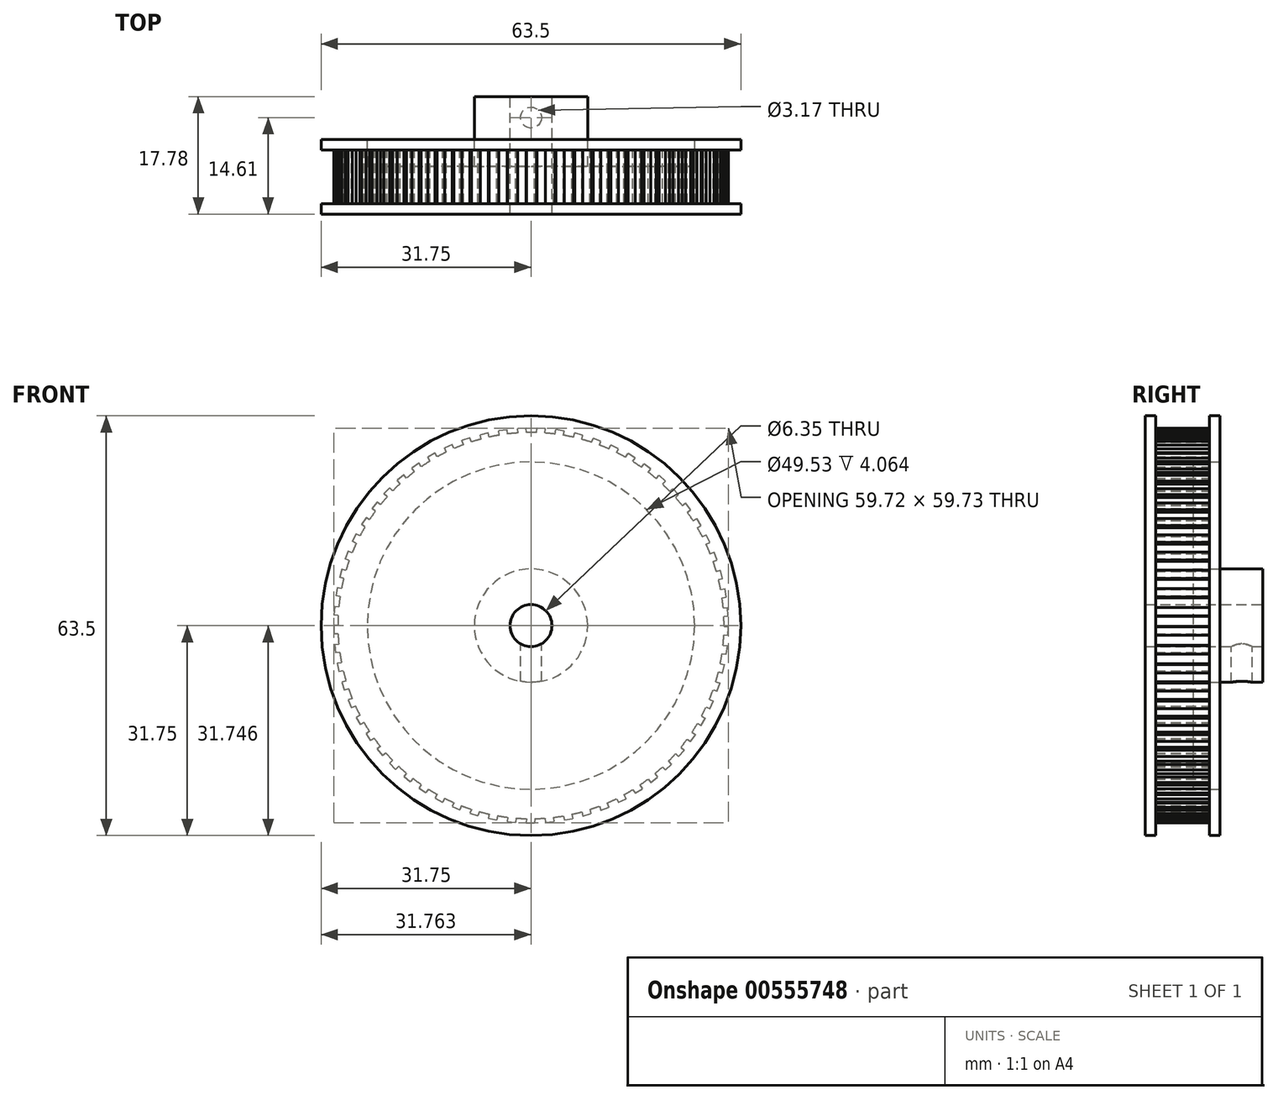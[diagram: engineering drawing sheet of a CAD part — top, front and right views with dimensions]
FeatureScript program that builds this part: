
annotation { "Feature Type Name" : "Feature", "Feature Type Description" : "" }
export const myFeature = defineFeature(function(context is Context, id is Id, definition is map)
    precondition{}
    {
        {
            var Q0;
            Q0=qCreatedBy(makeId("Front.planeOp"),FACE);
            var sketch = newSketch(context, id + "F0", { "sketchPlane" : qUnion([Q0])});
            skCircle(sketch, "E0", {"center": v(0, 0) * mm, "radius": 29.21 * mm});
            skSolve(sketch);
        }
        {
            var Q0;
            Q0=makeQuery(id+"F0.imprint","IMPRINT",FACE,{"disambiguationData":[TD([[makeQuery(id+"F0.imprint","IMPRINT",EDGE,{"derivedFrom":sQuery(id+"F0.wireOp",EDGE,"E0")}),1.0]])]});
            extrude(context, id + "F1", {"entities" : qUnion([Q0]), "depth" : 8.13 * mm, "offsetDistance" : 25.4 * mm});
        }
        {
            var Q0;
            Q0=makeQuery(id+"F1.opExtrude","CAP_FACE",FACE,{"disambiguationData":[OSD([sQuery(id+"F0.wireOp",EDGE,"E0")])],"isStart":true});
            var sketch = newSketch(context, id + "F2", { "sketchPlane" : qUnion([Q0])});
            skCircle(sketch, "E1", {"center": v(0, 0) * mm, "radius": 3.81 * mm});
            skSolve(sketch);
        }
        {
            var Q0;
            Q0=makeQuery(id+"F1.opExtrude","CAP_FACE",FACE,{"disambiguationData":[OSD([sQuery(id+"F0.wireOp",EDGE,"E0")])],"isStart":false});
            var sketch = newSketch(context, id + "F3", { "sketchPlane" : qUnion([Q0])});
            skCircle(sketch, "E2", {"center": v(0, 0) * mm, "radius": 31.75 * mm});
            skSolve(sketch);
        }
        {
            var Q0;
            Q0 = qSketchRegion(id + "F3", true);
            extrude(context, id + "F4", {"entities" : qUnion([Q0]), "operationType" : NewBodyOperationType.ADD, "depth" : 1.59 * mm, "offsetDistance" : 25.4 * mm});
        }
        {
            var Q0;
            Q0=makeQuery(id+"F1.opExtrude","CAP_FACE",FACE,{"disambiguationData":[OSD([sQuery(id+"F0.wireOp",EDGE,"E0")])],"isStart":true});
            var sketch = newSketch(context, id + "F5", { "sketchPlane" : qUnion([Q0])});
            skLineSegment(sketch, "E3.bottom", {"start": v(0, 0) * mm, "end": v(29.85, 0) * mm});
            skLineSegment(sketch, "E3.top", {"start": v(0, -1.27) * mm, "end": v(29.85, -1.27) * mm});
            skLineSegment(sketch, "E3.left", {"start": v(0, 0) * mm, "end": v(0, -1.27) * mm});
            skLineSegment(sketch, "E3.right", {"start": v(29.85, 0) * mm, "end": v(29.85, -1.27) * mm});
            skLineSegment(sketch, "E4.1.0", {"start": v(0.12, -1.26) * mm, "end": v(29.83, 1.62) * mm});
            skLineSegment(sketch, "E4.1.1", {"start": v(0, 0) * mm, "end": v(29.7, 2.88) * mm});
            skLineSegment(sketch, "E4.1.2", {"start": v(29.7, 2.88) * mm, "end": v(29.83, 1.62) * mm});
            skLineSegment(sketch, "E4.2.0", {"start": v(0.24, -1.25) * mm, "end": v(29.53, 4.49) * mm});
            skLineSegment(sketch, "E4.2.1", {"start": v(0, 0) * mm, "end": v(29.29, 5.73) * mm});
            skLineSegment(sketch, "E4.2.2", {"start": v(29.29, 5.73) * mm, "end": v(29.53, 4.49) * mm});
            skLineSegment(sketch, "E4.3.0", {"start": v(0.36, -1.22) * mm, "end": v(28.96, 7.32) * mm});
            skLineSegment(sketch, "E4.3.1", {"start": v(0, 0) * mm, "end": v(28.6, 8.53) * mm});
            skLineSegment(sketch, "E4.3.2", {"start": v(28.6, 8.53) * mm, "end": v(28.96, 7.32) * mm});
            skLineSegment(sketch, "E4.4.0", {"start": v(0.48, -1.18) * mm, "end": v(28.12, 10.08) * mm});
            skLineSegment(sketch, "E4.4.1", {"start": v(0, 0) * mm, "end": v(27.64, 11.25) * mm});
            skLineSegment(sketch, "E4.4.2", {"start": v(27.64, 11.25) * mm, "end": v(28.12, 10.08) * mm});
            skLineSegment(sketch, "E4.5.0", {"start": v(0.6, -1.12) * mm, "end": v(27.02, 12.75) * mm});
            skLineSegment(sketch, "E4.5.1", {"start": v(0, 0) * mm, "end": v(26.43, 13.87) * mm});
            skLineSegment(sketch, "E4.5.2", {"start": v(26.43, 13.87) * mm, "end": v(27.02, 12.75) * mm});
            skLineSegment(sketch, "E4.6.0", {"start": v(0.7, -1.06) * mm, "end": v(25.66, 15.3) * mm});
            skLineSegment(sketch, "E4.6.1", {"start": v(0, 0) * mm, "end": v(24.96, 16.36) * mm});
            skLineSegment(sketch, "E4.6.2", {"start": v(24.96, 16.36) * mm, "end": v(25.66, 15.3) * mm});
            skLineSegment(sketch, "E4.7.0", {"start": v(0.8, -1) * mm, "end": v(24.06, 17.7) * mm});
            skLineSegment(sketch, "E4.7.1", {"start": v(0, 0) * mm, "end": v(23.27, 18.69) * mm});
            skLineSegment(sketch, "E4.7.2", {"start": v(23.27, 18.69) * mm, "end": v(24.06, 17.7) * mm});
            skLineSegment(sketch, "E4.8.0", {"start": v(0.89, -0.9) * mm, "end": v(22.24, 19.94) * mm});
            skLineSegment(sketch, "E4.8.1", {"start": v(0, 0) * mm, "end": v(21.36, 20.85) * mm});
            skLineSegment(sketch, "E4.8.2", {"start": v(21.36, 20.85) * mm, "end": v(22.24, 19.94) * mm});
            skLineSegment(sketch, "E4.9.0", {"start": v(0.97, -0.82) * mm, "end": v(20.22, 22) * mm});
            skLineSegment(sketch, "E4.9.1", {"start": v(0, 0) * mm, "end": v(19.25, 22.81) * mm});
            skLineSegment(sketch, "E4.9.2", {"start": v(19.25, 22.81) * mm, "end": v(20.22, 22) * mm});
            skLineSegment(sketch, "E4.10.0", {"start": v(1.05, -0.72) * mm, "end": v(18, 23.84) * mm});
            skLineSegment(sketch, "E4.10.1", {"start": v(0, 0) * mm, "end": v(16.95, 24.56) * mm});
            skLineSegment(sketch, "E4.10.2", {"start": v(16.95, 24.56) * mm, "end": v(18, 23.84) * mm});
            skLineSegment(sketch, "E4.11.0", {"start": v(1.1, -0.62) * mm, "end": v(15.61, 25.47) * mm});
            skLineSegment(sketch, "E4.11.1", {"start": v(0, 0) * mm, "end": v(14.5, 26.08) * mm});
            skLineSegment(sketch, "E4.11.2", {"start": v(14.5, 26.08) * mm, "end": v(15.61, 25.47) * mm});
            skLineSegment(sketch, "E4.12.0", {"start": v(1.16, -0.5) * mm, "end": v(13.08, 26.85) * mm});
            skLineSegment(sketch, "E4.12.1", {"start": v(0, 0) * mm, "end": v(11.92, 27.36) * mm});
            skLineSegment(sketch, "E4.12.2", {"start": v(11.92, 27.36) * mm, "end": v(13.08, 26.85) * mm});
            skLineSegment(sketch, "E4.13.0", {"start": v(1.2, -0.4) * mm, "end": v(10.43, 28) * mm});
            skLineSegment(sketch, "E4.13.1", {"start": v(0, 0) * mm, "end": v(9.22, 28.38) * mm});
            skLineSegment(sketch, "E4.13.2", {"start": v(9.22, 28.38) * mm, "end": v(10.43, 28) * mm});
            skLineSegment(sketch, "E4.14.0", {"start": v(1.24, -0.27) * mm, "end": v(7.68, 28.87) * mm});
            skLineSegment(sketch, "E4.14.1", {"start": v(0, 0) * mm, "end": v(6.44, 29.14) * mm});
            skLineSegment(sketch, "E4.14.2", {"start": v(6.44, 29.14) * mm, "end": v(7.68, 28.87) * mm});
            skLineSegment(sketch, "E4.15.0", {"start": v(1.26, -0.15) * mm, "end": v(4.86, 29.47) * mm});
            skLineSegment(sketch, "E4.15.1", {"start": v(0, 0) * mm, "end": v(3.6, 29.63) * mm});
            skLineSegment(sketch, "E4.15.2", {"start": v(3.6, 29.63) * mm, "end": v(4.86, 29.47) * mm});
            skLineSegment(sketch, "E4.16.0", {"start": v(1.27, -0.03) * mm, "end": v(2, 29.8) * mm});
            skLineSegment(sketch, "E4.16.1", {"start": v(0, 0) * mm, "end": v(0.72, 29.84) * mm});
            skLineSegment(sketch, "E4.16.2", {"start": v(0.72, 29.84) * mm, "end": v(2, 29.8) * mm});
            skLineSegment(sketch, "E4.17.0", {"start": v(1.27, 0.1) * mm, "end": v(-0.9, 29.86) * mm});
            skLineSegment(sketch, "E4.17.1", {"start": v(0, 0) * mm, "end": v(-2.16, 29.77) * mm});
            skLineSegment(sketch, "E4.17.2", {"start": v(-2.16, 29.77) * mm, "end": v(-0.9, 29.86) * mm});
            skLineSegment(sketch, "E4.18.0", {"start": v(1.25, 0.21) * mm, "end": v(-3.77, 29.63) * mm});
            skLineSegment(sketch, "E4.18.1", {"start": v(0, 0) * mm, "end": v(-5.02, 29.42) * mm});
            skLineSegment(sketch, "E4.18.2", {"start": v(-5.02, 29.42) * mm, "end": v(-3.77, 29.63) * mm});
            skLineSegment(sketch, "E4.19.0", {"start": v(1.23, 0.33) * mm, "end": v(-6.62, 29.13) * mm});
            skLineSegment(sketch, "E4.19.1", {"start": v(0, 0) * mm, "end": v(-7.84, 28.8) * mm});
            skLineSegment(sketch, "E4.19.2", {"start": v(-7.84, 28.8) * mm, "end": v(-6.62, 29.13) * mm});
            skLineSegment(sketch, "E4.20.0", {"start": v(1.19, 0.45) * mm, "end": v(-9.4, 28.36) * mm});
            skLineSegment(sketch, "E4.20.1", {"start": v(0, 0) * mm, "end": v(-10.58, 27.9) * mm});
            skLineSegment(sketch, "E4.20.2", {"start": v(-10.58, 27.9) * mm, "end": v(-9.4, 28.36) * mm});
            skLineSegment(sketch, "E4.21.0", {"start": v(1.14, 0.56) * mm, "end": v(-12.09, 27.32) * mm});
            skLineSegment(sketch, "E4.21.1", {"start": v(0, 0) * mm, "end": v(-13.23, 26.75) * mm});
            skLineSegment(sketch, "E4.21.2", {"start": v(-13.23, 26.75) * mm, "end": v(-12.09, 27.32) * mm});
            skLineSegment(sketch, "E4.22.0", {"start": v(1.08, 0.67) * mm, "end": v(-14.67, 26.02) * mm});
            skLineSegment(sketch, "E4.22.1", {"start": v(0, 0) * mm, "end": v(-15.75, 25.35) * mm});
            skLineSegment(sketch, "E4.22.2", {"start": v(-15.75, 25.35) * mm, "end": v(-14.67, 26.02) * mm});
            skLineSegment(sketch, "E4.23.0", {"start": v(1, 0.77) * mm, "end": v(-17.11, 24.49) * mm});
            skLineSegment(sketch, "E4.23.1", {"start": v(0, 0) * mm, "end": v(-18.12, 23.71) * mm});
            skLineSegment(sketch, "E4.23.2", {"start": v(-18.12, 23.71) * mm, "end": v(-17.11, 24.49) * mm});
            skLineSegment(sketch, "E4.24.0", {"start": v(0.93, 0.86) * mm, "end": v(-19.4, 22.72) * mm});
            skLineSegment(sketch, "E4.24.1", {"start": v(0, 0) * mm, "end": v(-20.32, 21.85) * mm});
            skLineSegment(sketch, "E4.24.2", {"start": v(-20.32, 21.85) * mm, "end": v(-19.4, 22.72) * mm});
            skLineSegment(sketch, "E4.25.0", {"start": v(0.84, 0.95) * mm, "end": v(-21.5, 20.74) * mm});
            skLineSegment(sketch, "E4.25.1", {"start": v(0, 0) * mm, "end": v(-22.34, 19.8) * mm});
            skLineSegment(sketch, "E4.25.2", {"start": v(-22.34, 19.8) * mm, "end": v(-21.5, 20.74) * mm});
            skLineSegment(sketch, "E4.26.0", {"start": v(0.75, 1.03) * mm, "end": v(-23.4, 18.57) * mm});
            skLineSegment(sketch, "E4.26.1", {"start": v(0, 0) * mm, "end": v(-24.15, 17.54) * mm});
            skLineSegment(sketch, "E4.26.2", {"start": v(-24.15, 17.54) * mm, "end": v(-23.4, 18.57) * mm});
            skLineSegment(sketch, "E4.27.0", {"start": v(0.64, 1.1) * mm, "end": v(-25.08, 16.22) * mm});
            skLineSegment(sketch, "E4.27.1", {"start": v(0, 0) * mm, "end": v(-25.73, 15.13) * mm});
            skLineSegment(sketch, "E4.27.2", {"start": v(-25.73, 15.13) * mm, "end": v(-25.08, 16.22) * mm});
            skLineSegment(sketch, "E4.28.0", {"start": v(0.54, 1.15) * mm, "end": v(-26.53, 13.73) * mm});
            skLineSegment(sketch, "E4.28.1", {"start": v(0, 0) * mm, "end": v(-27.07, 12.58) * mm});
            skLineSegment(sketch, "E4.28.2", {"start": v(-27.07, 12.58) * mm, "end": v(-26.53, 13.73) * mm});
            skLineSegment(sketch, "E4.29.0", {"start": v(0.42, 1.2) * mm, "end": v(-27.73, 11.1) * mm});
            skLineSegment(sketch, "E4.29.1", {"start": v(0, 0) * mm, "end": v(-28.15, 9.9) * mm});
            skLineSegment(sketch, "E4.29.2", {"start": v(-28.15, 9.9) * mm, "end": v(-27.73, 11.1) * mm});
            skLineSegment(sketch, "E4.30.0", {"start": v(0.3, 1.23) * mm, "end": v(-28.67, 8.38) * mm});
            skLineSegment(sketch, "E4.30.1", {"start": v(0, 0) * mm, "end": v(-28.98, 7.14) * mm});
            skLineSegment(sketch, "E4.30.2", {"start": v(-28.98, 7.14) * mm, "end": v(-28.67, 8.38) * mm});
            skLineSegment(sketch, "E4.31.0", {"start": v(0.18, 1.26) * mm, "end": v(-29.35, 5.57) * mm});
            skLineSegment(sketch, "E4.31.1", {"start": v(0, 0) * mm, "end": v(-29.53, 4.31) * mm});
            skLineSegment(sketch, "E4.31.2", {"start": v(-29.53, 4.31) * mm, "end": v(-29.35, 5.57) * mm});
            skLineSegment(sketch, "E4.32.0", {"start": v(0.06, 1.27) * mm, "end": v(-29.75, 2.71) * mm});
            skLineSegment(sketch, "E4.32.1", {"start": v(0, 0) * mm, "end": v(-29.81, 1.44) * mm});
            skLineSegment(sketch, "E4.32.2", {"start": v(-29.81, 1.44) * mm, "end": v(-29.75, 2.71) * mm});
            skLineSegment(sketch, "E4.33.0", {"start": v(-0.06, 1.27) * mm, "end": v(-29.87, -0.17) * mm});
            skLineSegment(sketch, "E4.33.1", {"start": v(0, 0) * mm, "end": v(-29.81, -1.44) * mm});
            skLineSegment(sketch, "E4.33.2", {"start": v(-29.81, -1.44) * mm, "end": v(-29.87, -0.17) * mm});
            skLineSegment(sketch, "E4.34.0", {"start": v(-0.18, 1.26) * mm, "end": v(-29.72, -3.06) * mm});
            skLineSegment(sketch, "E4.34.1", {"start": v(0, 0) * mm, "end": v(-29.53, -4.31) * mm});
            skLineSegment(sketch, "E4.34.2", {"start": v(-29.53, -4.31) * mm, "end": v(-29.72, -3.06) * mm});
            skLineSegment(sketch, "E4.35.0", {"start": v(-0.3, 1.23) * mm, "end": v(-29.28, -5.9) * mm});
            skLineSegment(sketch, "E4.35.1", {"start": v(0, 0) * mm, "end": v(-28.98, -7.14) * mm});
            skLineSegment(sketch, "E4.35.2", {"start": v(-28.98, -7.14) * mm, "end": v(-29.28, -5.9) * mm});
            skLineSegment(sketch, "E4.36.0", {"start": v(-0.42, 1.2) * mm, "end": v(-28.57, -8.7) * mm});
            skLineSegment(sketch, "E4.36.1", {"start": v(0, 0) * mm, "end": v(-28.15, -9.9) * mm});
            skLineSegment(sketch, "E4.36.2", {"start": v(-28.15, -9.9) * mm, "end": v(-28.57, -8.7) * mm});
            skLineSegment(sketch, "E4.37.0", {"start": v(-0.54, 1.15) * mm, "end": v(-27.6, -11.42) * mm});
            skLineSegment(sketch, "E4.37.1", {"start": v(0, 0) * mm, "end": v(-27.07, -12.58) * mm});
            skLineSegment(sketch, "E4.37.2", {"start": v(-27.07, -12.58) * mm, "end": v(-27.6, -11.42) * mm});
            skLineSegment(sketch, "E4.38.0", {"start": v(-0.64, 1.1) * mm, "end": v(-26.37, -14.04) * mm});
            skLineSegment(sketch, "E4.38.1", {"start": v(0, 0) * mm, "end": v(-25.73, -15.13) * mm});
            skLineSegment(sketch, "E4.38.2", {"start": v(-25.73, -15.13) * mm, "end": v(-26.37, -14.04) * mm});
            skLineSegment(sketch, "E4.39.0", {"start": v(-0.75, 1.03) * mm, "end": v(-24.9, -16.51) * mm});
            skLineSegment(sketch, "E4.39.1", {"start": v(0, 0) * mm, "end": v(-24.15, -17.54) * mm});
            skLineSegment(sketch, "E4.39.2", {"start": v(-24.15, -17.54) * mm, "end": v(-24.9, -16.51) * mm});
            skLineSegment(sketch, "E4.40.0", {"start": v(-0.84, 0.95) * mm, "end": v(-23.18, -18.84) * mm});
            skLineSegment(sketch, "E4.40.1", {"start": v(0, 0) * mm, "end": v(-22.34, -19.8) * mm});
            skLineSegment(sketch, "E4.40.2", {"start": v(-22.34, -19.8) * mm, "end": v(-23.18, -18.84) * mm});
            skLineSegment(sketch, "E4.41.0", {"start": v(-0.93, 0.86) * mm, "end": v(-21.25, -20.99) * mm});
            skLineSegment(sketch, "E4.41.1", {"start": v(0, 0) * mm, "end": v(-20.32, -21.85) * mm});
            skLineSegment(sketch, "E4.41.2", {"start": v(-20.32, -21.85) * mm, "end": v(-21.25, -20.99) * mm});
            skLineSegment(sketch, "E4.42.0", {"start": v(-1, 0.77) * mm, "end": v(-19.13, -22.94) * mm});
            skLineSegment(sketch, "E4.42.1", {"start": v(0, 0) * mm, "end": v(-18.12, -23.71) * mm});
            skLineSegment(sketch, "E4.42.2", {"start": v(-18.12, -23.71) * mm, "end": v(-19.13, -22.94) * mm});
            skLineSegment(sketch, "E4.43.0", {"start": v(-1.08, 0.67) * mm, "end": v(-16.83, -24.68) * mm});
            skLineSegment(sketch, "E4.43.1", {"start": v(0, 0) * mm, "end": v(-15.75, -25.35) * mm});
            skLineSegment(sketch, "E4.43.2", {"start": v(-15.75, -25.35) * mm, "end": v(-16.83, -24.68) * mm});
            skLineSegment(sketch, "E4.44.0", {"start": v(-1.14, 0.56) * mm, "end": v(-14.37, -26.2) * mm});
            skLineSegment(sketch, "E4.44.1", {"start": v(0, 0) * mm, "end": v(-13.23, -26.75) * mm});
            skLineSegment(sketch, "E4.44.2", {"start": v(-13.23, -26.75) * mm, "end": v(-14.37, -26.2) * mm});
            skLineSegment(sketch, "E4.45.0", {"start": v(-1.19, 0.45) * mm, "end": v(-11.77, -27.46) * mm});
            skLineSegment(sketch, "E4.45.1", {"start": v(0, 0) * mm, "end": v(-10.58, -27.9) * mm});
            skLineSegment(sketch, "E4.45.2", {"start": v(-10.58, -27.9) * mm, "end": v(-11.77, -27.46) * mm});
            skLineSegment(sketch, "E4.46.0", {"start": v(-1.23, 0.33) * mm, "end": v(-9.07, -28.46) * mm});
            skLineSegment(sketch, "E4.46.1", {"start": v(0, 0) * mm, "end": v(-7.84, -28.8) * mm});
            skLineSegment(sketch, "E4.46.2", {"start": v(-7.84, -28.8) * mm, "end": v(-9.07, -28.46) * mm});
            skLineSegment(sketch, "E4.47.0", {"start": v(-1.25, 0.21) * mm, "end": v(-6.28, -29.2) * mm});
            skLineSegment(sketch, "E4.47.1", {"start": v(0, 0) * mm, "end": v(-5.02, -29.42) * mm});
            skLineSegment(sketch, "E4.47.2", {"start": v(-5.02, -29.42) * mm, "end": v(-6.28, -29.2) * mm});
            skLineSegment(sketch, "E4.48.0", {"start": v(-1.27, 0.1) * mm, "end": v(-3.43, -29.67) * mm});
            skLineSegment(sketch, "E4.48.1", {"start": v(0, 0) * mm, "end": v(-2.16, -29.77) * mm});
            skLineSegment(sketch, "E4.48.2", {"start": v(-2.16, -29.77) * mm, "end": v(-3.43, -29.67) * mm});
            skLineSegment(sketch, "E4.49.0", {"start": v(-1.27, -0.03) * mm, "end": v(-0.55, -29.87) * mm});
            skLineSegment(sketch, "E4.49.1", {"start": v(0, 0) * mm, "end": v(0.72, -29.84) * mm});
            skLineSegment(sketch, "E4.49.2", {"start": v(0.72, -29.84) * mm, "end": v(-0.55, -29.87) * mm});
            skLineSegment(sketch, "E4.50.0", {"start": v(-1.26, -0.15) * mm, "end": v(2.34, -29.78) * mm});
            skLineSegment(sketch, "E4.50.1", {"start": v(0, 0) * mm, "end": v(3.6, -29.63) * mm});
            skLineSegment(sketch, "E4.50.2", {"start": v(3.6, -29.63) * mm, "end": v(2.34, -29.78) * mm});
            skLineSegment(sketch, "E4.51.0", {"start": v(-1.24, -0.27) * mm, "end": v(5.2, -29.42) * mm});
            skLineSegment(sketch, "E4.51.1", {"start": v(0, 0) * mm, "end": v(6.44, -29.14) * mm});
            skLineSegment(sketch, "E4.51.2", {"start": v(6.44, -29.14) * mm, "end": v(5.2, -29.42) * mm});
            skLineSegment(sketch, "E4.52.0", {"start": v(-1.2, -0.4) * mm, "end": v(8.01, -28.78) * mm});
            skLineSegment(sketch, "E4.52.1", {"start": v(0, 0) * mm, "end": v(9.22, -28.38) * mm});
            skLineSegment(sketch, "E4.52.2", {"start": v(9.22, -28.38) * mm, "end": v(8.01, -28.78) * mm});
            skLineSegment(sketch, "E4.53.0", {"start": v(-1.16, -0.5) * mm, "end": v(10.75, -27.87) * mm});
            skLineSegment(sketch, "E4.53.1", {"start": v(0, 0) * mm, "end": v(11.92, -27.36) * mm});
            skLineSegment(sketch, "E4.53.2", {"start": v(11.92, -27.36) * mm, "end": v(10.75, -27.87) * mm});
            skLineSegment(sketch, "E4.54.0", {"start": v(-1.1, -0.62) * mm, "end": v(13.4, -26.7) * mm});
            skLineSegment(sketch, "E4.54.1", {"start": v(0, 0) * mm, "end": v(14.5, -26.08) * mm});
            skLineSegment(sketch, "E4.54.2", {"start": v(14.5, -26.08) * mm, "end": v(13.4, -26.7) * mm});
            skLineSegment(sketch, "E4.55.0", {"start": v(-1.05, -0.72) * mm, "end": v(15.9, -25.28) * mm});
            skLineSegment(sketch, "E4.55.1", {"start": v(0, 0) * mm, "end": v(16.95, -24.56) * mm});
            skLineSegment(sketch, "E4.55.2", {"start": v(16.95, -24.56) * mm, "end": v(15.9, -25.28) * mm});
            skLineSegment(sketch, "E4.56.0", {"start": v(-0.97, -0.82) * mm, "end": v(18.27, -23.63) * mm});
            skLineSegment(sketch, "E4.56.1", {"start": v(0, 0) * mm, "end": v(19.25, -22.81) * mm});
            skLineSegment(sketch, "E4.56.2", {"start": v(19.25, -22.81) * mm, "end": v(18.27, -23.63) * mm});
            skLineSegment(sketch, "E4.57.0", {"start": v(-0.89, -0.9) * mm, "end": v(20.47, -21.76) * mm});
            skLineSegment(sketch, "E4.57.1", {"start": v(0, 0) * mm, "end": v(21.36, -20.85) * mm});
            skLineSegment(sketch, "E4.57.2", {"start": v(21.36, -20.85) * mm, "end": v(20.47, -21.76) * mm});
            skLineSegment(sketch, "E4.58.0", {"start": v(-0.8, -1) * mm, "end": v(22.47, -19.68) * mm});
            skLineSegment(sketch, "E4.58.1", {"start": v(0, 0) * mm, "end": v(23.27, -18.69) * mm});
            skLineSegment(sketch, "E4.58.2", {"start": v(23.27, -18.69) * mm, "end": v(22.47, -19.68) * mm});
            skLineSegment(sketch, "E4.59.0", {"start": v(-0.7, -1.06) * mm, "end": v(24.27, -17.42) * mm});
            skLineSegment(sketch, "E4.59.1", {"start": v(0, 0) * mm, "end": v(24.96, -16.36) * mm});
            skLineSegment(sketch, "E4.59.2", {"start": v(24.96, -16.36) * mm, "end": v(24.27, -17.42) * mm});
            skLineSegment(sketch, "E4.60.0", {"start": v(-0.6, -1.12) * mm, "end": v(25.84, -15) * mm});
            skLineSegment(sketch, "E4.60.1", {"start": v(0, 0) * mm, "end": v(26.43, -13.87) * mm});
            skLineSegment(sketch, "E4.60.2", {"start": v(26.43, -13.87) * mm, "end": v(25.84, -15) * mm});
            skLineSegment(sketch, "E4.61.0", {"start": v(-0.48, -1.18) * mm, "end": v(27.16, -12.43) * mm});
            skLineSegment(sketch, "E4.61.1", {"start": v(0, 0) * mm, "end": v(27.64, -11.25) * mm});
            skLineSegment(sketch, "E4.61.2", {"start": v(27.64, -11.25) * mm, "end": v(27.16, -12.43) * mm});
            skLineSegment(sketch, "E4.62.0", {"start": v(-0.36, -1.22) * mm, "end": v(28.24, -9.75) * mm});
            skLineSegment(sketch, "E4.62.1", {"start": v(0, 0) * mm, "end": v(28.6, -8.53) * mm});
            skLineSegment(sketch, "E4.62.2", {"start": v(28.6, -8.53) * mm, "end": v(28.24, -9.75) * mm});
            skLineSegment(sketch, "E4.63.0", {"start": v(-0.24, -1.25) * mm, "end": v(29.04, -6.98) * mm});
            skLineSegment(sketch, "E4.63.1", {"start": v(0, 0) * mm, "end": v(29.29, -5.73) * mm});
            skLineSegment(sketch, "E4.63.2", {"start": v(29.29, -5.73) * mm, "end": v(29.04, -6.98) * mm});
            skLineSegment(sketch, "E4.64.0", {"start": v(-0.12, -1.26) * mm, "end": v(29.58, -4.14) * mm});
            skLineSegment(sketch, "E4.64.1", {"start": v(0, 0) * mm, "end": v(29.7, -2.88) * mm});
            skLineSegment(sketch, "E4.64.2", {"start": v(29.7, -2.88) * mm, "end": v(29.58, -4.14) * mm});
            skPoint(sketch, "E4.center", {"position": v(0, 0) * mm});
            skSolve(sketch);
        }
        {
            var Q0;
            Q0 = qSketchRegion(id + "F5", true);
            var Q1;
            Q1=makeQuery(id+"F4.opExtrude","CAP_FACE",FACE,{"disambiguationData":[OSD([sQuery(id+"F3.wireOp",EDGE,"E2")])],"isStart":true});
            extrude(context, id + "F6", {"entities" : qUnion([Q0]), "operationType" : NewBodyOperationType.ADD, "endBound" : BoundingType.UP_TO_SURFACE, "oppositeDirection" : true, "depth" : 25.4 * mm, "endBoundEntityFace" : qUnion([Q1]), "offsetDistance" : 25.4 * mm});
        }
        {
            var Q0;
            Q0=makeQuery(id+"F2.imprint","IMPRINT",FACE,{"disambiguationData":[TD([[makeQuery(id+"F2.imprint","IMPRINT",EDGE,{"derivedFrom":sQuery(id+"F2.wireOp",EDGE,"E1")}),-1.0]])]});
            var sketch = newSketch(context, id + "F7", { "sketchPlane" : qUnion([Q0])});
            skCircle(sketch, "E5", {"center": v(0, 0) * mm, "radius": 31.75 * mm});
            skSolve(sketch);
        }
        {
            var Q0;
            Q0 = qSketchRegion(id + "F7", true);
            extrude(context, id + "F8", {"entities" : qUnion([Q0]), "operationType" : NewBodyOperationType.ADD, "depth" : 1.59 * mm, "offsetDistance" : 25.4 * mm});
        }
        {
            var Q0;
            Q0=makeQuery(id+"F8.opExtrude","CAP_FACE",FACE,{"disambiguationData":[OSD([sQuery(id+"F7.wireOp",EDGE,"E5")])],"isStart":false});
            var sketch = newSketch(context, id + "F9", { "sketchPlane" : qUnion([Q0])});
            skCircle(sketch, "E6", {"center": v(0, 0) * mm, "radius": 3.18 * mm});
            skSolve(sketch);
        }
        {
            var Q0;
            Q0 = qSketchRegion(id + "F9", true);
            extrude(context, id + "F10", {"entities" : qUnion([Q0]), "operationType" : NewBodyOperationType.REMOVE, "oppositeDirection" : true, "depth" : 25.4 * mm, "offsetDistance" : 25.4 * mm});
        }
        {
            var Q0;
            Q0=makeQuery(id+"F8.opExtrude","CAP_FACE",FACE,{"disambiguationData":[OSD([sQuery(id+"F7.wireOp",EDGE,"E5")])],"isStart":false});
            var sketch = newSketch(context, id + "F11", { "sketchPlane" : qUnion([Q0])});
            skCircle(sketch, "E7", {"center": v(0, 0) * mm, "radius": 24.77 * mm});
            skCircle(sketch, "E8", {"center": v(0, 0) * mm, "radius": 8.57 * mm});
            skSolve(sketch);
        }
        {
            var Q0;
            Q0=makeQuery(id+"F11.imprint","IMPRINT",FACE,{"disambiguationData":[TD([[makeQuery(id+"F11.imprint","IMPRINT",EDGE,{"derivedFrom":sQuery(id+"F11.wireOp",EDGE,"E7")}),1.0]])]});
            extrude(context, id + "F12", {"entities" : qUnion([Q0]), "operationType" : NewBodyOperationType.REMOVE, "oppositeDirection" : true, "depth" : 4.06 * mm, "offsetDistance" : 25.4 * mm});
        }
        {
            var Q0;
            Q0=makeQuery(id+"F12.boolean.opBoolean","SPLIT",FACE,{"disambiguationData":[TD([makeQuery(id+"F10.boolean.opBoolean","COPY",FACE,{"derivedFrom":makeQuery(id+"F10.opExtrude","SWEPT_FACE",FACE,{"disambiguationData":[OSD([sQuery(id+"F9.wireOp",EDGE,"E6")])]})})])],"derivedFrom":makeQuery(id+"F8.opExtrude","CAP_FACE",FACE,{"disambiguationData":[OSD([sQuery(id+"F7.wireOp",EDGE,"E5")])],"isStart":false})});
            extrude(context, id + "F13", {"entities" : qUnion([Q0]), "operationType" : NewBodyOperationType.ADD, "depth" : 6.48 * mm, "offsetDistance" : 25.4 * mm});
        }
        {
            var Q0;
            Q0=qCreatedBy(makeId("Top.planeOp"),FACE);
            var sketch = newSketch(context, id + "F14", { "sketchPlane" : qUnion([Q0])});
            skCircle(sketch, "E9", {"center": v(0, 4.89) * mm, "radius": 1.59 * mm});
            skSolve(sketch);
        }
        {
            var Q0;
            Q0=makeQuery(id+"F14.imprint","IMPRINT",FACE,{"disambiguationData":[TD([[makeQuery(id+"F14.imprint","IMPRINT",EDGE,{"derivedFrom":sQuery(id+"F14.wireOp",EDGE,"E9")}),1.0]])]});
            extrude(context, id + "F15", {"entities" : qUnion([Q0]), "operationType" : NewBodyOperationType.REMOVE, "oppositeDirection" : true, "depth" : 25.4 * mm, "offsetDistance" : 25.4 * mm});
        }
    });
